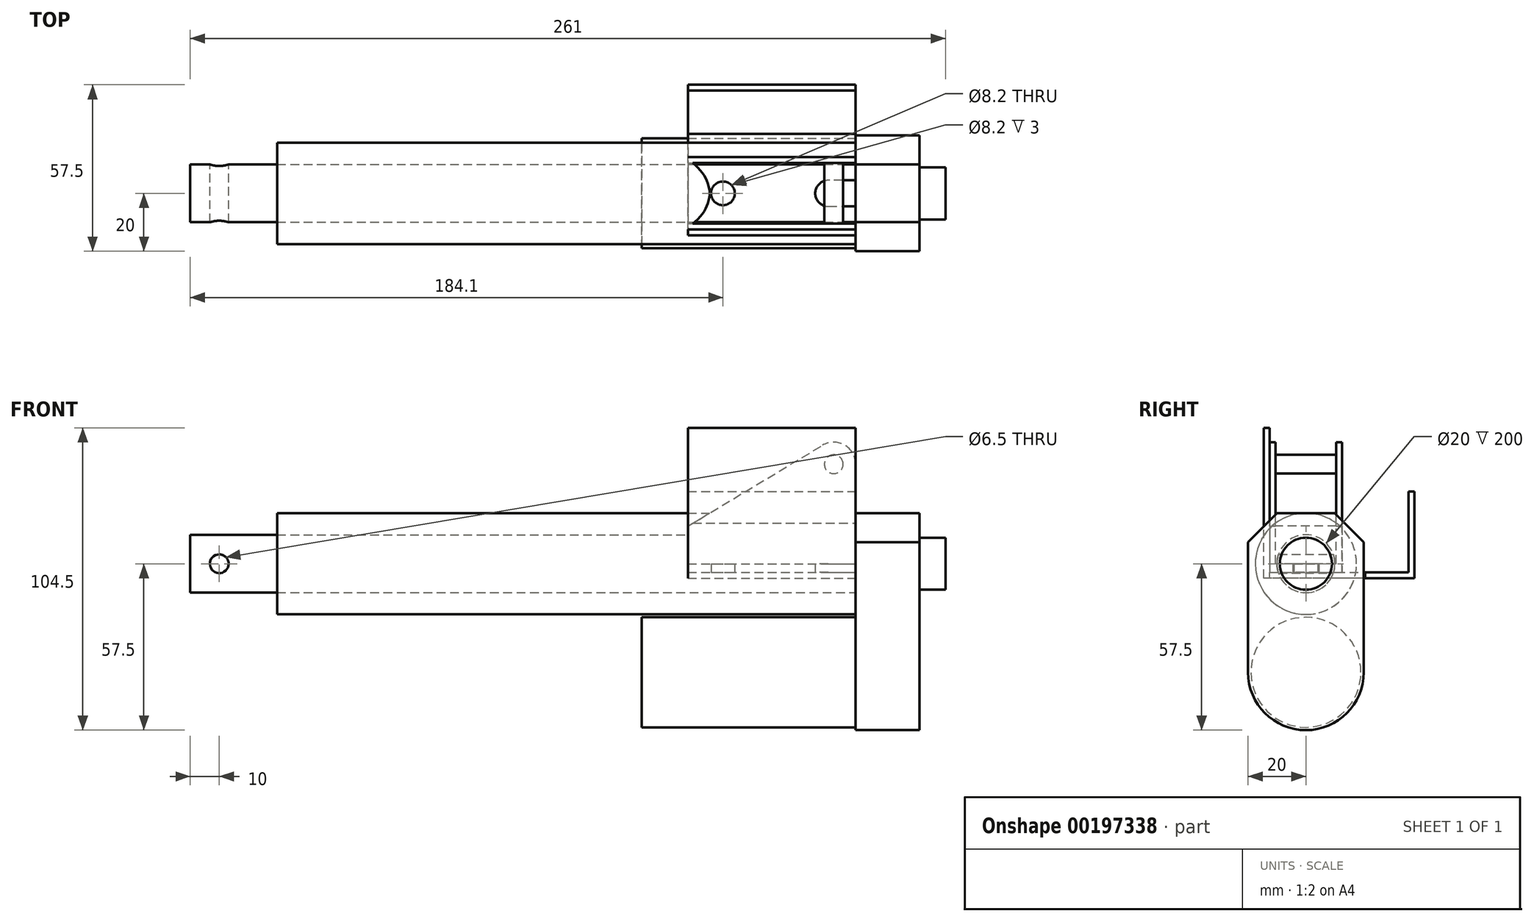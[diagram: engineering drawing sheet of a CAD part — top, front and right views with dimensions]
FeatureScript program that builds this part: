
annotation { "Feature Type Name" : "Feature", "Feature Type Description" : "" }
export const myFeature = defineFeature(function(context is Context, id is Id, definition is map)
    precondition{}
    {
        {
            assignVariable(context, id + "F0", {"name" : "actuator_stroke", "anyValue" : 150});
        }
        {
            assignVariable(context, id + "F1", {"name" : "actuator_rod_dia", "anyValue" : 20});
        }
        {
            var Q0;
            Q0=qCreatedBy(makeId("Right.planeOp"),FACE);
            var sketch = newSketch(context, id + "F2", { "sketchPlane" : qUnion([Q0])});
            skLineSegment(sketch, "E0", {"start": v(-20, 7.5) * mm, "end": v(-20, -37.5) * mm});
            skLineSegment(sketch, "E1", {"start": v(20, -37.5) * mm, "end": v(20, 7.5) * mm});
            skLineSegment(sketch, "E2", {"start": v(-20, 7.5) * mm, "end": v(-10, 17.5) * mm});
            skLineSegment(sketch, "E3", {"start": v(-10, 17.5) * mm, "end": v(10, 17.5) * mm});
            skLineSegment(sketch, "E4", {"start": v(10, 17.5) * mm, "end": v(20, 7.5) * mm});
            skArc(sketch, "E5", {"start": v(-20, -37.5) * mm, "mid": v(0, -57.5) * mm, "end": v(20, -37.5) * mm});
            skCircle(sketch, "E6", {"center": v(0, -37.5) * mm, "radius": 19 * mm});
            skCircle(sketch, "E7", {"center": v(0, 0) * mm, "radius": 17.5 * mm});
            skCircle(sketch, "E8", {"center": v(0, 0) * mm, "radius": 10 * mm});
            skCircle(sketch, "E9", {"center": v(0, 0) * mm, "radius": 9 * mm});
            skSolve(sketch);
        }
        {
            var Q0;
            Q0=qSketchRegion(id+"F2",true);
            var Q1;
            Q1=makeQuery(id+"F2.imprint","IMPRINT",FACE,{"disambiguationData":[TD([[makeQuery(id+"F2.imprint","IMPRINT",EDGE,{"derivedFrom":sQuery(id+"F2.wireOp",EDGE,"E6")}),1.0]])]});
            var Q2;
            Q2=makeQuery(id+"F2.imprint","IMPRINT",FACE,{"disambiguationData":[TD([[makeQuery(id+"F2.imprint","IMPRINT",EDGE,{"derivedFrom":sQuery(id+"F2.wireOp",EDGE,"E9")}),1.0]])]});
            var Q3;
            Q3=makeQuery(id+"F2.imprint","IMPRINT",FACE,{"disambiguationData":[TD([[makeQuery(id+"F2.imprint","IMPRINT",EDGE,{"derivedFrom":sQuery(id+"F2.wireOp",EDGE,"E8")}),1.0]])]});
            extrude(context, id + "F3", {"entities" : qUnion([Q0, Q1, Q2, Q3]), "depth" : 22 * mm});
        }
        {
            var Q0;
            Q0=makeQuery(id+"F2.imprint","IMPRINT",FACE,{"disambiguationData":[TD([[makeQuery(id+"F2.imprint","IMPRINT",EDGE,{"derivedFrom":sQuery(id+"F2.wireOp",EDGE,"E6")}),1.0]])]});
            extrude(context, id + "F4", {"entities" : qUnion([Q0]), "operationType" : NewBodyOperationType.ADD, "oppositeDirection" : true, "depth" : 74 * mm});
        }
        {
            var Q0;
            Q0=makeQuery(id+"F2.imprint","IMPRINT",FACE,{"disambiguationData":[TD([[makeQuery(id+"F2.imprint","IMPRINT",EDGE,{"derivedFrom":sQuery(id+"F2.wireOp",EDGE,"E7")}),1.0]])]});
            extrude(context, id + "F5", {"entities" : qUnion([Q0]), "operationType" : NewBodyOperationType.ADD, "oppositeDirection" : true, "depth" : (getVariable(context, 'actuator_stroke') + 50) * mm});
        }
        {
            var Q0;
            Q0=makeQuery(id+"F2.imprint","IMPRINT",FACE,{"disambiguationData":[TD([[makeQuery(id+"F2.imprint","IMPRINT",EDGE,{"derivedFrom":sQuery(id+"F2.wireOp",EDGE,"E9")}),1.0]])]});
            extrude(context, id + "F6", {"entities" : qUnion([Q0]), "operationType" : NewBodyOperationType.ADD, "depth" : 31 * mm});
        }
        {
            var Q0;
            Q0=qCreatedBy(makeId("Right.planeOp"),FACE);
            var sketch = newSketch(context, id + "F7", { "sketchPlane" : qUnion([Q0])});
            skCircle(sketch, "E10", {"center": v(0, 0) * mm, "radius": 10 * mm});
            skSolve(sketch);
        }
        {
            var Q0;
            Q0=qSketchRegion(id+"F7",true);
            extrude(context, id + "F8", {"entities" : qUnion([Q0]), "oppositeDirection" : true, "depth" : (getVariable(context, 'actuator_stroke') + 50 + 20 + 10) * mm});
        }
        {
            var Q0;
            Q0=qCreatedBy(makeId("Front.planeOp"),FACE);
            var sketch = newSketch(context, id + "F9", { "sketchPlane" : qUnion([Q0])});
            skCircle(sketch, "E11", {"center": v(-220, 0) * mm, "radius": 3.25 * mm});
            skSolve(sketch);
        }
        {
            var Q0;
            Q0=qSketchRegion(id+"F9",true);
            extrude(context, id + "F10", {"entities" : qUnion([Q0]), "operationType" : NewBodyOperationType.REMOVE, "depth" : (getVariable(context, 'actuator_rod_dia')) * mm, "symmetric" : true});
        }
        {
            var Q0;
            Q0=qCreatedBy(makeId("Front.planeOp"),FACE);
            var sketch = newSketch(context, id + "F11", { "sketchPlane" : qUnion([Q0])});
            skCircle(sketch, "E12", {"center": v(40, 0) * mm, "radius": 3.25 * mm});
            skSolve(sketch);
        }
        {
            var Q0;
            Q0=qSketchRegion(id+"F11",true);
            extrude(context, id + "F12", {"entities" : qUnion([Q0]), "operationType" : NewBodyOperationType.REMOVE, "oppositeDirection" : true, "depth" : (getVariable(context, 'actuator_rod_dia')) * mm, "symmetric" : true});
        }
        {
            var Q0;
            Q0=qCreatedBy(makeId("Front.planeOp"),FACE);
            var sketch = newSketch(context, id + "F13", { "sketchPlane" : qUnion([Q0])});
            skLineSegment(sketch, "E13", {"start": v(0, 0) * mm, "end": v(0, 34.4) * mm});
            skLineSegment(sketch, "E14", {"start": v(-58, 0) * mm, "end": v(-58, -3) * mm});
            skLineSegment(sketch, "E15", {"start": v(-58, -3) * mm, "end": v(0, -3) * mm});
            skLineSegment(sketch, "E16", {"start": v(0, -3) * mm, "end": v(0, 0) * mm});
            skPoint(sketch, "E17.visualSharp", {"position": v(0, 51.26) * mm});
            skArc(sketch, "E17.filletArc", {"start": v(0, 34.4) * mm, "mid": v(-3.86, 41.01) * mm, "end": v(-11.51, 40.92) * mm});
            skCircle(sketch, "E18", {"center": v(-7.6, 34.4) * mm, "radius": 3.25 * mm});
            skLineSegment(sketch, "E19", {"start": v(-58, 0) * mm, "end": v(0, 0) * mm});
            skLineSegment(sketch, "E20", {"start": v(-58, 0) * mm, "end": v(-58, 13) * mm});
            skLineSegment(sketch, "E21", {"start": v(-58, 13) * mm, "end": v(-11.51, 40.92) * mm});
            skSolve(sketch);
        }
        {
            var Q0;
            Q0=qSketchRegion(id+"F13",true);
            extrude(context, id + "F14", {"entities" : qUnion([Q0]), "depth" : (getVariable(context, 'actuator_rod_dia') + 4 + 1) * mm, "symmetric" : true});
        }
        {
            var Q0;
            Q0=makeQuery(id+"F13.imprint","IMPRINT",FACE,{"disambiguationData":[TD([[makeQuery(id+"F13.imprint","IMPRINT",EDGE,{"derivedFrom":sQuery(id+"F13.wireOp",EDGE,"E13")}),1.0]])]});
            extrude(context, id + "F15", {"entities" : qUnion([Q0]), "operationType" : NewBodyOperationType.REMOVE, "oppositeDirection" : true, "depth" : (getVariable(context, 'actuator_rod_dia') + 1) * mm, "symmetric" : true});
        }
        {
            var Q0;
            Q0=makeQuery(id+"F13.imprint","IMPRINT",FACE,{"disambiguationData":[TD([[makeQuery(id+"F13.imprint","IMPRINT",EDGE,{"derivedFrom":sQuery(id+"F13.wireOp",EDGE,"E18")}),1.0]])]});
            extrude(context, id + "F16", {"entities" : qUnion([Q0]), "operationType" : NewBodyOperationType.ADD, "depth" : (getVariable(context, 'actuator_rod_dia') + 4 + 1) * mm, "symmetric" : true});
        }
        {
            var Q0;
            Q0=makeQuery(id+"F14.opExtrude","SWEPT_FACE",FACE,{"disambiguationData":[OSD([sQuery(id+"F13.wireOp",EDGE,"E13"),sQuery(id+"F13.wireOp",EDGE,"E16")])]});
            var sketch = newSketch(context, id + "F17", { "sketchPlane" : qUnion([Q0])});
            skLineSegment(sketch, "E22", {"start": v(20.5, -5) * mm, "end": v(-14.5, -5) * mm});
            skLineSegment(sketch, "E23", {"start": v(-14.5, -5) * mm, "end": v(-14.5, 47) * mm});
            skLineSegment(sketch, "E24", {"start": v(-14.5, 47) * mm, "end": v(-12.5, 47) * mm});
            skLineSegment(sketch, "E25", {"start": v(-12.5, 47) * mm, "end": v(-12.5, -3) * mm});
            skLineSegment(sketch, "E26", {"start": v(-12.5, -3) * mm, "end": v(20.5, -3) * mm});
            skLineSegment(sketch, "E27", {"start": v(20.5, -3) * mm, "end": v(20.5, -5) * mm});
            skSolve(sketch);
        }
        {
            var Q0;
            Q0=qSketchRegion(id+"F17",true);
            extrude(context, id + "F18", {"entities" : qUnion([Q0]), "oppositeDirection" : true, "depth" : 58 * mm});
        }
        {
            var Q0;
            Q0=makeQuery(id+"F14.opExtrude","SWEPT_FACE",FACE,{"disambiguationData":[OSD([sQuery(id+"F13.wireOp",EDGE,"E13"),sQuery(id+"F13.wireOp",EDGE,"E16")])]});
            var sketch = newSketch(context, id + "F19", { "sketchPlane" : qUnion([Q0])});
            skLineSegment(sketch, "E28", {"start": v(-12.5, 34.4) * mm, "end": v(-12.5, -3) * mm});
            skLineSegment(sketch, "E29", {"start": v(-12.5, -3) * mm, "end": v(35.5, -3) * mm});
            skLineSegment(sketch, "E30", {"start": v(35.5, -3) * mm, "end": v(35.5, 25) * mm});
            skLineSegment(sketch, "E31", {"start": v(35.5, 25) * mm, "end": v(37.5, 25) * mm});
            skLineSegment(sketch, "E32", {"start": v(37.5, 25) * mm, "end": v(37.5, -5) * mm});
            skLineSegment(sketch, "E33", {"start": v(37.5, -5) * mm, "end": v(-12.5, -5) * mm});
            skLineSegment(sketch, "E34", {"start": v(-12.5, -5) * mm, "end": v(-12.5, -3) * mm});
            skSolve(sketch);
        }
        {
            var Q0;
            {var subQ2=sQuery(id+"F19.wireOp",EDGE,"E30");Q0=makeQuery(id+"F19.imprint","IMPRINT",FACE,{"disambiguationData":[TD([[makeQuery(id+"F19.imprint","IMPRINT",EDGE,{"derivedFrom":subQ2}),-1.0]])]});}
            extrude(context, id + "F20", {"entities" : qUnion([Q0]), "oppositeDirection" : true, "depth" : 58 * mm});
        }
        {
            var Q0;
            Q0=makeQuery(id+"F14.opExtrude","SWEPT_FACE",FACE,{"disambiguationData":[OSD([sQuery(id+"F13.wireOp",EDGE,"E15")])]});
            var sketch = newSketch(context, id + "F21", { "sketchPlane" : qUnion([Q0])});
            skCircle(sketch, "E35", {"center": v(-45.9, 0) * mm, "radius": 4.1 * mm});
            skArc(sketch, "E36", {"start": v(-9.5, 4.5) * mm, "mid": v(-14, 0) * mm, "end": v(-9.5, -4.5) * mm});
            skLineSegment(sketch, "E37", {"start": v(-9.5, 4.5) * mm, "end": v(0, 4.5) * mm});
            skLineSegment(sketch, "E38", {"start": v(0, 4.5) * mm, "end": v(0, -4.5) * mm});
            skLineSegment(sketch, "E39", {"start": v(0, -4.5) * mm, "end": v(-9.5, -4.5) * mm});
            skSolve(sketch);
        }
        {
            var Q0;
            Q0 = qSketchRegion(id + "F21", true);
            extrude(context, id + "F22", {"entities" : qUnion([Q0]), "operationType" : NewBodyOperationType.REMOVE, "oppositeDirection" : true, "depth" : 5 * mm});
        }
    });
